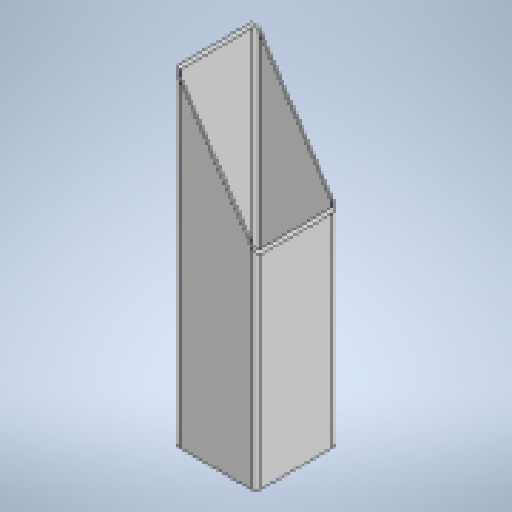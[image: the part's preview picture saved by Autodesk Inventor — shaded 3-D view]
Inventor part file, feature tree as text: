
AUTODESK INVENTOR PART (.ipt)
format: ipt  version: 2025 (Build 290162010, 162A)  size: 162,816 bytes
history: native  units: mm
features: extrude x2, sketch x2
ambient origin geometry x8: Origin, YZ Plane, XZ Plane, XY Plane, X Axis, Y Axis, Z Axis, Center Point
bodies: Solid1 (feature_tree)
feature tree (4):
  extrude  "Extrusion1"  Depth=5.0mm
  extrude  "Extrusion2"  Depth=2.0mm TaperAngle=0.0deg
  sketch  "Sketch1"  dims[d0=80.0mm d1=5.0mm]
  sketch  "Sketch2"  dims[d2=2.0mm d3=320.0mm d4=0.0mm d5=21.544344mm d6=0.0mm d7=0.0mm]
